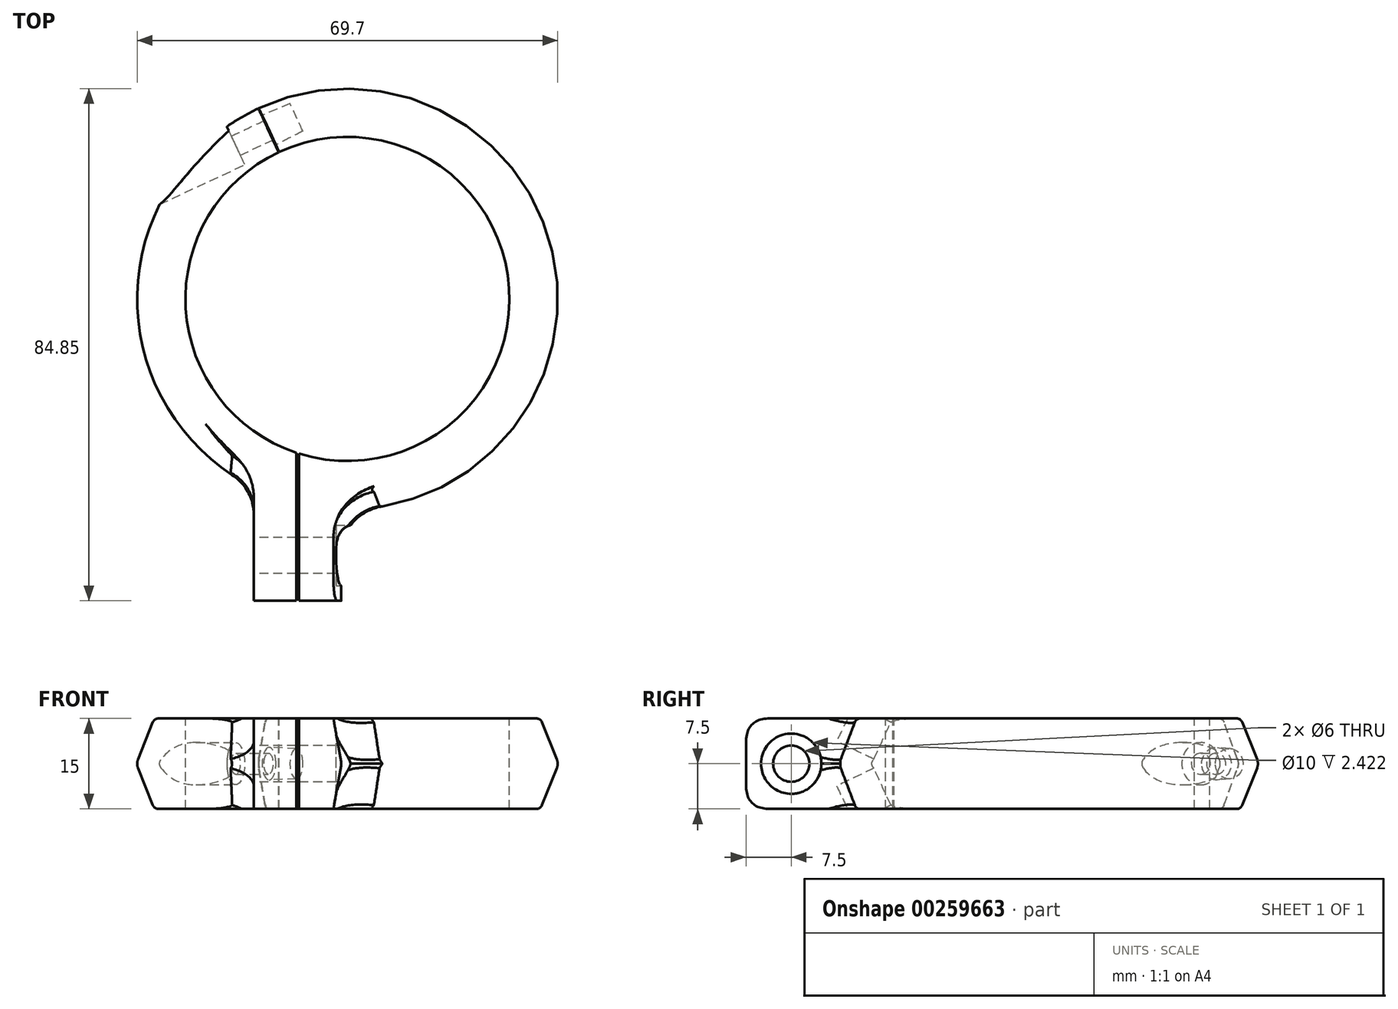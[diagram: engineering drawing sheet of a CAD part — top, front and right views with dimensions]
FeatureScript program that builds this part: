
annotation { "Feature Type Name" : "Feature", "Feature Type Description" : "" }
export const myFeature = defineFeature(function(context is Context, id is Id, definition is map)
    precondition{}
    {
        {
            var Q0;
            Q0=qCreatedBy(makeId("Front.planeOp"),FACE);
            var sketch = newSketch(context, id + "F0", { "sketchPlane" : qUnion([Q0])});
            skLineSegment(sketch, "E0.bottom", {"start": v(0, 7.5) * mm, "end": v(32, 7.5) * mm});
            skLineSegment(sketch, "E0.top", {"start": v(0, -7.5) * mm, "end": v(32, -7.5) * mm});
            skLineSegment(sketch, "E0.left", {"start": v(0, 7.5) * mm, "end": v(0, -7.5) * mm});
            skLineSegment(sketch, "E1", {"start": v(32, 7.5) * mm, "end": v(35, 0) * mm});
            skLineSegment(sketch, "E2", {"start": v(35, 0) * mm, "end": v(32, -7.5) * mm});
            skLineSegment(sketch, "E3", {"start": v(0, 0) * mm, "end": v(0, 25.95) * mm, "construction": true});
            skSolve(sketch);
        }
        {
            var Q0;
            Q0 = qSketchRegion(id + "F0", true);
            var Q1;
            Q1=sQuery(id+"F0.wireOp",EDGE,"E3");
            revolve(context, id + "F1", {"entities" : qUnion([Q0]), "axis" : qUnion([Q1]), "revolveType" : RevolveType.FULL});
        }
        {
            var Q0;
            Q0=makeQuery(id+"F1.opRevolve","SWEPT_EDGE",EDGE,{"disambiguationData":[OSD([sQuery(id+"F0.wireOp",EDGE,"E1"),sQuery(id+"F0.wireOp",EDGE,"E2")])]});
            fillet(context, id + "F2", {"entities" : qUnion([Q0]), "radius" : 2 * mm, "tangentPropagation" : true, "allowEdgeOverflow" : false});
        }
        {
            var Q0;
            {var subQ0=sQuery(id+"F0.wireOp",EDGE,"E1");var subQ1=sQuery(id+"F0.wireOp",EDGE,"E0.bottom");Q0=makeQuery(id+"F13.boolean.opBoolean","SPLIT",EDGE,{"disambiguationData":[TD([makeQuery(id+"F5.opExtrude","SWEPT_FACE",FACE,{"disambiguationData":[OSD([sQuery(id+"F4.wireOp",EDGE,"E7")])]})])],"derivedFrom":makeQuery(id+"F1.opRevolve","SWEPT_EDGE",EDGE,{"disambiguationData":[OSD([subQ1,subQ0])]})});}
            var Q1;
            Q1=makeQuery(id+"F1.opRevolve","SWEPT_EDGE",EDGE,{"disambiguationData":[OSD([sQuery(id+"F0.wireOp",EDGE,"E0.top"),sQuery(id+"F0.wireOp",EDGE,"E2")])]});
            fillet(context, id + "F3", {"entities" : qUnion([Q0, Q1]), "radius" : 1 * mm, "tangentPropagation" : true, "allowEdgeOverflow" : false});
        }
        {
            var Q0;
            Q0=qCreatedBy(makeId("Front.planeOp"),FACE);
            var sketch = newSketch(context, id + "F4", { "sketchPlane" : qUnion([Q0])});
            skLineSegment(sketch, "E4.bottom", {"start": v(-15.5, 7.5) * mm, "end": v(-1, 7.5) * mm});
            skLineSegment(sketch, "E4.top", {"start": v(-15.5, -7.5) * mm, "end": v(-1, -7.5) * mm});
            skLineSegment(sketch, "E4.left", {"start": v(-15.5, 7.5) * mm, "end": v(-15.5, -7.5) * mm});
            skLineSegment(sketch, "E4.right", {"start": v(-1, 7.5) * mm, "end": v(-1, -7.5) * mm, "construction": true});
            skLineSegment(sketch, "E5", {"start": v(-15.5, 0) * mm, "end": v(-14.18, 7.5) * mm, "construction": true});
            skLineSegment(sketch, "E6", {"start": v(-15.5, 0) * mm, "end": v(-14.18, -7.5) * mm, "construction": true});
            skLineSegment(sketch, "E7", {"start": v(-1, 0) * mm, "end": v(-2.32, 7.5) * mm});
            skLineSegment(sketch, "E8", {"start": v(-1, 0) * mm, "end": v(-2.32, -7.5) * mm});
            skSolve(sketch);
        }
        {
            var Q0;
            Q0 = qSketchRegion(id + "F4", true);
            extrude(context, id + "F5", {"entities" : qUnion([Q0]), "operationType" : NewBodyOperationType.ADD, "depth" : 50 * mm});
        }
        {
            var Q0;
            Q0=qCreatedBy(makeId("Top.planeOp"),FACE);
            var sketch = newSketch(context, id + "F6", { "sketchPlane" : qUnion([Q0])});
            skCircle(sketch, "E9", {"center": v(0, 0) * mm, "radius": 26.85 * mm});
            skSolve(sketch);
        }
        {
            var Q0;
            Q0 = qSketchRegion(id + "F6", true);
            extrude(context, id + "F7", {"entities" : qUnion([Q0]), "operationType" : NewBodyOperationType.REMOVE, "endBound" : BoundingType.SYMMETRIC, "oppositeDirection" : true, "depth" : 25 * mm});
        }
        {
            var Q0;
            Q0=qCreatedBy(makeId("Right.planeOp"),FACE);
            var sketch = newSketch(context, id + "F8", { "sketchPlane" : qUnion([Q0])});
            skLineSegment(sketch, "E10", {"start": v(25, 5) * mm, "end": v(26.85, 5) * mm});
            skLineSegment(sketch, "E11", {"start": v(26.85, 5) * mm, "end": v(28.67, 0) * mm});
            skLineSegment(sketch, "E12", {"start": v(28.67, 0) * mm, "end": v(26.85, -5) * mm});
            skLineSegment(sketch, "E13", {"start": v(26.85, -5) * mm, "end": v(25, -5) * mm});
            skLineSegment(sketch, "E14", {"start": v(25, -5) * mm, "end": v(25, 5) * mm});
            skLineSegment(sketch, "E15", {"start": v(0, 0) * mm, "end": v(0, 25.99) * mm, "construction": true});
            skSolve(sketch);
        }
        {
            var Q0;
            Q0=makeQuery(id+"F5.boolean.opBoolean","MERGE",FACE,{"derivedFrom":[makeQuery(id+"F1.opRevolve","SWEPT_FACE",FACE,{"disambiguationData":[OSD([sQuery(id+"F0.wireOp",EDGE,"E0.bottom")])]}),makeQuery(id+"F5.opExtrude","SWEPT_FACE",FACE,{"disambiguationData":[OSD([sQuery(id+"F4.wireOp",EDGE,"E4.bottom")])]})]});
            var sketch = newSketch(context, id + "F9", { "sketchPlane" : qUnion([Q0])});
            skLineSegment(sketch, "E16", {"start": v(0, 0) * mm, "end": v(-15.5, -31.05) * mm, "construction": true});
            skSolve(sketch);
        }
        {
            var Q0;
            Q0=sQuery(id+"F9.wireOp",EDGE,"E16");
            cPlane(context, id + "F10", {"entities" : qUnion([Q0]), "cplaneType" : CPlaneType.LINE_ANGLE, "offset" : 25 * mm, "angle" : 90 * degree, "width" : 150 * mm, "height" : 150 * mm});
        }
        {
            var Q0;
            Q0=qCreatedBy(id+"F10.planeOp",FACE);
            var sketch = newSketch(context, id + "F11", { "sketchPlane" : qUnion([Q0])});
            skLineSegment(sketch, "E17", {"start": v(-25, -5) * mm, "end": v(-26.85, -5) * mm});
            skLineSegment(sketch, "E18", {"start": v(-26.85, -5) * mm, "end": v(-28.67, 0) * mm});
            skLineSegment(sketch, "E19", {"start": v(-28.67, 0) * mm, "end": v(-26.85, 5) * mm});
            skLineSegment(sketch, "E20", {"start": v(-26.85, 5) * mm, "end": v(-25, 5) * mm});
            skLineSegment(sketch, "E21", {"start": v(-25, 5) * mm, "end": v(-25, -5) * mm});
            skLineSegment(sketch, "E22", {"start": v(0, 0) * mm, "end": v(0, 25.99) * mm, "construction": true});
            skSolve(sketch);
        }
        {
            var Q0;
            Q0=qCreatedBy(makeId("Top.planeOp"),FACE);
            var sketch = newSketch(context, id + "F12", { "sketchPlane" : qUnion([Q0])});
            skLineSegment(sketch, "E23", {"start": v(0, 0) * mm, "end": v(-9.92, 21.28) * mm, "construction": true});
            skLineSegment(sketch, "E24.bottom", {"start": v(-10.28, 22.17) * mm, "end": v(-10.38, 22.13) * mm});
            skLineSegment(sketch, "E24.top", {"start": v(-15.21, 32.74) * mm, "end": v(-15.3, 32.7) * mm});
            skLineSegment(sketch, "E24.left", {"start": v(-10.28, 22.17) * mm, "end": v(-15.21, 32.74) * mm});
            skLineSegment(sketch, "E24.right", {"start": v(-10.38, 22.13) * mm, "end": v(-15.3, 32.7) * mm});
            skPoint(sketch, "E24.middle", {"position": v(-12.8, 27.44) * mm});
            skLineSegment(sketch, "E25.bottom", {"start": v(-8.5, -51.4) * mm, "end": v(-8, -51.4) * mm});
            skLineSegment(sketch, "E25.top", {"start": v(-8.5, -23.49) * mm, "end": v(-8, -23.49) * mm});
            skLineSegment(sketch, "E25.left", {"start": v(-8.5, -51.4) * mm, "end": v(-8.5, -23.49) * mm});
            skLineSegment(sketch, "E25.right", {"start": v(-8, -51.4) * mm, "end": v(-8, -23.49) * mm});
            skSolve(sketch);
        }
        {
            var Q0;
            Q0 = qSketchRegion(id + "F12", true);
            extrude(context, id + "F13", {"entities" : qUnion([Q0]), "operationType" : NewBodyOperationType.REMOVE, "endBound" : BoundingType.SYMMETRIC, "oppositeDirection" : true, "depth" : 25 * mm});
        }
        {
            var Q0;
            Q0=makeQuery(id+"F5.boolean.opBoolean","INTERSECT",EDGE,{"derivedFrom":[makeQuery(id+"F1.opRevolve","SWEPT_FACE",FACE,{"disambiguationData":[OSD([sQuery(id+"F0.wireOp",EDGE,"E2")])]}),makeQuery(id+"F5.opExtrude","SWEPT_FACE",FACE,{"disambiguationData":[OSD([sQuery(id+"F4.wireOp",EDGE,"E4.left")])]})]});
            var Q1;
            Q1=makeQuery(id+"F5.boolean.opBoolean","INTERSECT",EDGE,{"derivedFrom":[makeQuery(id+"F1.opRevolve","SWEPT_FACE",FACE,{"disambiguationData":[OSD([sQuery(id+"F0.wireOp",EDGE,"E1")])]}),makeQuery(id+"F5.opExtrude","SWEPT_FACE",FACE,{"disambiguationData":[OSD([sQuery(id+"F4.wireOp",EDGE,"E4.left")])]})]});
            var Q2;
            Q2=makeQuery(id+"F5.boolean.opBoolean","INTERSECT",EDGE,{"derivedFrom":[makeQuery(id+"F1.opRevolve","SWEPT_FACE",FACE,{"disambiguationData":[OSD([sQuery(id+"F0.wireOp",EDGE,"E1")])]}),makeQuery(id+"F5.opExtrude","SWEPT_FACE",FACE,{"disambiguationData":[OSD([sQuery(id+"F4.wireOp",EDGE,"E4.left")])]})]});
            var Q3;
            Q3=makeQuery(id+"F5.boolean.opBoolean","INTERSECT",EDGE,{"derivedFrom":[makeQuery(id+"F1.opRevolve","SWEPT_FACE",FACE,{"disambiguationData":[OSD([sQuery(id+"F0.wireOp",EDGE,"E1")])]}),makeQuery(id+"F5.opExtrude","SWEPT_FACE",FACE,{"disambiguationData":[OSD([sQuery(id+"F4.wireOp",EDGE,"E7")])]})]});
            var Q4;
            Q4=makeQuery(id+"F5.boolean.opBoolean","INTERSECT",EDGE,{"derivedFrom":[makeQuery(id+"F1.opRevolve","SWEPT_FACE",FACE,{"disambiguationData":[OSD([sQuery(id+"F0.wireOp",EDGE,"E2")])]}),makeQuery(id+"F5.opExtrude","SWEPT_FACE",FACE,{"disambiguationData":[OSD([sQuery(id+"F4.wireOp",EDGE,"E8")])]})]});
            fillet(context, id + "F14", {"entities" : qUnion([Q0, Q1, Q2, Q3, Q4]), "radius" : 8 * mm, "tangentPropagation" : true, "allowEdgeOverflow" : false});
        }
        {
            var Q0;
            Q0=makeQuery(id+"F13.boolean.opBoolean","COPY",FACE,{"derivedFrom":makeQuery(id+"F13.opExtrude","SWEPT_FACE",FACE,{"disambiguationData":[OSD([sQuery(id+"F12.wireOp",EDGE,"E24.left")])]})});
            var sketch = newSketch(context, id + "F15", { "sketchPlane" : qUnion([Q0])});
            skCircle(sketch, "E26", {"center": v(-30.85, 0) * mm, "radius": 2.7 * mm});
            skLineSegment(sketch, "E27", {"start": v(-26.85, 0) * mm, "end": v(-34.85, 0) * mm, "construction": true});
            skSolve(sketch);
        }
        {
            var Q0;
            Q0=makeQuery(id+"F15.imprint","IMPRINT",FACE,{"disambiguationData":[TD([[makeQuery(id+"F15.imprint","IMPRINT",EDGE,{"derivedFrom":sQuery(id+"F15.wireOp",EDGE,"E26")}),1.0]])]});
            extrude(context, id + "F16", {"entities" : qUnion([Q0]), "operationType" : NewBodyOperationType.REMOVE, "oppositeDirection" : true, "depth" : 5 * mm, "hasDraft" : true, "draftAngle" : 2 * degree, "draftPullDirection" : true});
        }
        {
            var Q0;
            Q0=makeQuery(id+"F13.boolean.opBoolean","COPY",FACE,{"derivedFrom":makeQuery(id+"F13.opExtrude","SWEPT_FACE",FACE,{"disambiguationData":[OSD([sQuery(id+"F12.wireOp",EDGE,"E24.right")])]})});
            var sketch = newSketch(context, id + "F17", { "sketchPlane" : qUnion([Q0])});
            skLineSegment(sketch, "E28", {"start": v(26.85, 0) * mm, "end": v(34.85, 0) * mm, "construction": true});
            skCircle(sketch, "E29", {"center": v(30.85, 0) * mm, "radius": 1.75 * mm});
            skSolve(sketch);
        }
        {
            var Q0;
            Q0 = qSketchRegion(id + "F17", true);
            extrude(context, id + "F18", {"entities" : qUnion([Q0]), "operationType" : NewBodyOperationType.REMOVE, "oppositeDirection" : true, "depth" : 6 * mm});
        }
        {
            var Q0;
            Q0=makeQuery(id+"F18.boolean.opBoolean","COPY",FACE,{"derivedFrom":makeQuery(id+"F18.opExtrude","CAP_FACE",FACE,{"disambiguationData":[OSD([sQuery(id+"F17.wireOp",EDGE,"E29")])],"isStart":false})});
            var sketch = newSketch(context, id + "F19", { "sketchPlane" : qUnion([Q0])});
            skCircle(sketch, "E30", {"center": v(30.85, 0) * mm, "radius": 3.5 * mm});
            skSolve(sketch);
        }
        {
            var Q0;
            Q0 = qSketchRegion(id + "F19", true);
            extrude(context, id + "F20", {"entities" : qUnion([Q0]), "operationType" : NewBodyOperationType.REMOVE, "endBound" : BoundingType.THROUGH_ALL, "oppositeDirection" : true, "depth" : 25 * mm});
        }
        {
            var Q0;
            Q0=makeQuery(id+"F13.boolean.opBoolean","COPY",FACE,{"derivedFrom":makeQuery(id+"F13.opExtrude","SWEPT_FACE",FACE,{"disambiguationData":[OSD([sQuery(id+"F12.wireOp",EDGE,"E25.right")])]})});
            var sketch = newSketch(context, id + "F21", { "sketchPlane" : qUnion([Q0])});
            skCircle(sketch, "E31", {"center": v(42.5, 0) * mm, "radius": 3 * mm});
            skSolve(sketch);
        }
        {
            var Q0;
            Q0 = qSketchRegion(id + "F21", true);
            extrude(context, id + "F22", {"entities" : qUnion([Q0]), "operationType" : NewBodyOperationType.REMOVE, "endBound" : BoundingType.SYMMETRIC, "oppositeDirection" : true, "depth" : 25 * mm});
        }
        {
            var Q0;
            {var subQ0=sQuery(id+"F21.wireOp",EDGE,"TPeSEbKZ-4Bs4-KLaG-X3M5-nI107J7NiBt1");var subQ1=sQuery(id+"F4.wireOp",EDGE,"E4.bottom");var subQ2=sQuery(id+"F0.wireOp",EDGE,"E0.bottom");Q0=makeQuery(id+"F22.boolean.opBoolean","COPY",EDGE,{"disambiguationData":[TD([makeQuery(id+"F5.opExtrude","SWEPT_FACE",FACE,{"disambiguationData":[OSD([sQuery(id+"F4.wireOp",EDGE,"E5")])]})])],"derivedFrom":makeQuery(id+"F22.opExtrude","SWEPT_EDGE",EDGE,{"disambiguationData":[OSD([subQ2,subQ1,sQuery(id+"F12.wireOp",EDGE,"E25.right"),subQ0,sQuery(id+"F21.wireOp",EDGE,"c0wj6FnS-jEuf-wRoK-qYGN-INKrLgW8l8Zs")])]})});}
            var Q1;
            {var subQ0=sQuery(id+"F12.wireOp",EDGE,"E25.right");var subQ1=sQuery(id+"F4.wireOp",EDGE,"E4.bottom");var subQ2=sQuery(id+"F0.wireOp",EDGE,"E0.bottom");var subQ3=sQuery(id+"F21.wireOp",EDGE,"TPeSEbKZ-4Bs4-KLaG-X3M5-nI107J7NiBt1");Q1=makeQuery(id+"F22.boolean.opBoolean","COPY",EDGE,{"disambiguationData":[TD([makeQuery(id+"F5.opExtrude","SWEPT_FACE",FACE,{"disambiguationData":[OSD([sQuery(id+"F4.wireOp",EDGE,"E7")])]})])],"derivedFrom":makeQuery(id+"F22.opExtrude","SWEPT_EDGE",EDGE,{"disambiguationData":[OSD([subQ2,subQ1,subQ0,subQ3,sQuery(id+"F21.wireOp",EDGE,"c0wj6FnS-jEuf-wRoK-qYGN-INKrLgW8l8Zs")])]})});}
            var Q2;
            {var subQ0=sQuery(id+"F21.wireOp",EDGE,"TPeSEbKZ-4Bs4-KLaG-X3M5-nI107J7NiBt1");var subQ1=sQuery(id+"F12.wireOp",EDGE,"E25.right");var subQ2=sQuery(id+"F4.wireOp",EDGE,"E8");var subQ3=sQuery(id+"F4.wireOp",EDGE,"E7");var subQ4=sQuery(id+"F21.wireOp",EDGE,"iLccIwtf-qxlF-KUq4-O1UZ-VWjskxav2twh");Q2=makeQuery(id+"F22.boolean.opBoolean","COPY",EDGE,{"disambiguationData":[TD([makeQuery(id+"F5.opExtrude","SWEPT_FACE",FACE,{"disambiguationData":[OSD([subQ3])]})])],"derivedFrom":makeQuery(id+"F22.opExtrude","SWEPT_EDGE",EDGE,{"disambiguationData":[OSD([sQuery(id+"F4.wireOp",EDGE,"E4.bottom"),sQuery(id+"F4.wireOp",EDGE,"E4.top"),sQuery(id+"F4.wireOp",EDGE,"E5"),sQuery(id+"F4.wireOp",EDGE,"E6"),subQ3,subQ2,subQ1,subQ0,subQ4])]})});}
            var Q3;
            {var subQ0=sQuery(id+"F21.wireOp",EDGE,"TPeSEbKZ-4Bs4-KLaG-X3M5-nI107J7NiBt1");var subQ1=sQuery(id+"F4.wireOp",EDGE,"E6");var subQ2=sQuery(id+"F4.wireOp",EDGE,"E5");var subQ3=sQuery(id+"F21.wireOp",EDGE,"iLccIwtf-qxlF-KUq4-O1UZ-VWjskxav2twh");Q3=makeQuery(id+"F22.boolean.opBoolean","COPY",EDGE,{"disambiguationData":[TD([makeQuery(id+"F5.opExtrude","SWEPT_FACE",FACE,{"disambiguationData":[OSD([subQ2])]})])],"derivedFrom":makeQuery(id+"F22.opExtrude","SWEPT_EDGE",EDGE,{"disambiguationData":[OSD([sQuery(id+"F4.wireOp",EDGE,"E4.bottom"),sQuery(id+"F4.wireOp",EDGE,"E4.top"),subQ2,subQ1,sQuery(id+"F4.wireOp",EDGE,"E7"),sQuery(id+"F4.wireOp",EDGE,"E8"),sQuery(id+"F12.wireOp",EDGE,"E25.right"),subQ0,subQ3])]})});}
            var Q4;
            {var subQ0=sQuery(id+"F4.wireOp",EDGE,"E4.top");var subQ1=sQuery(id+"F0.wireOp",EDGE,"E0.top");var subQ2=sQuery(id+"F21.wireOp",EDGE,"iLccIwtf-qxlF-KUq4-O1UZ-VWjskxav2twh");Q4=makeQuery(id+"F22.boolean.opBoolean","COPY",EDGE,{"disambiguationData":[TD([makeQuery(id+"F5.opExtrude","SWEPT_FACE",FACE,{"disambiguationData":[OSD([sQuery(id+"F4.wireOp",EDGE,"E6")])]})])],"derivedFrom":makeQuery(id+"F22.opExtrude","SWEPT_EDGE",EDGE,{"disambiguationData":[OSD([subQ1,subQ0,sQuery(id+"F12.wireOp",EDGE,"E25.right"),subQ2,sQuery(id+"F21.wireOp",EDGE,"4cMrprGq-YRgF-T9sy-pwaC-qQGlX6H42zO3")])]})});}
            var Q5;
            {var subQ0=sQuery(id+"F12.wireOp",EDGE,"E25.right");var subQ1=sQuery(id+"F4.wireOp",EDGE,"E4.top");var subQ2=sQuery(id+"F0.wireOp",EDGE,"E0.top");var subQ3=sQuery(id+"F21.wireOp",EDGE,"iLccIwtf-qxlF-KUq4-O1UZ-VWjskxav2twh");Q5=makeQuery(id+"F22.boolean.opBoolean","COPY",EDGE,{"disambiguationData":[TD([makeQuery(id+"F5.opExtrude","SWEPT_FACE",FACE,{"disambiguationData":[OSD([sQuery(id+"F4.wireOp",EDGE,"E8")])]})])],"derivedFrom":makeQuery(id+"F22.opExtrude","SWEPT_EDGE",EDGE,{"disambiguationData":[OSD([subQ2,subQ1,subQ0,subQ3,sQuery(id+"F21.wireOp",EDGE,"4cMrprGq-YRgF-T9sy-pwaC-qQGlX6H42zO3")])]})});}
            var Q6;
            Q6=makeQuery(id+"F5.opExtrude","SWEPT_EDGE",EDGE,{"disambiguationData":[OSD([sQuery(id+"F4.wireOp",EDGE,"E7"),sQuery(id+"F4.wireOp",EDGE,"E8")])]});
            var Q7;
            {var subQ0=sQuery(id+"F21.wireOp",EDGE,"TPeSEbKZ-4Bs4-KLaG-X3M5-nI107J7NiBt1");var subQ1=sQuery(id+"F4.wireOp",EDGE,"E4.bottom");var subQ2=sQuery(id+"F0.wireOp",EDGE,"E0.bottom");Q7=makeQuery(id+"F22.boolean.opBoolean","COPY",EDGE,{"disambiguationData":[TD([makeQuery(id+"F5.opExtrude","SWEPT_FACE",FACE,{"disambiguationData":[OSD([sQuery(id+"F4.wireOp",EDGE,"E4.left")])]})])],"derivedFrom":makeQuery(id+"F22.opExtrude","SWEPT_EDGE",EDGE,{"disambiguationData":[OSD([subQ2,subQ1,sQuery(id+"F12.wireOp",EDGE,"E25.right"),subQ0,sQuery(id+"F21.wireOp",EDGE,"c0wj6FnS-jEuf-wRoK-qYGN-INKrLgW8l8Zs")])]})});}
            var Q8;
            {var subQ0=sQuery(id+"F4.wireOp",EDGE,"E4.left");var subQ1=sQuery(id+"F21.wireOp",EDGE,"TPeSEbKZ-4Bs4-KLaG-X3M5-nI107J7NiBt1");var subQ2=sQuery(id+"F21.wireOp",EDGE,"iLccIwtf-qxlF-KUq4-O1UZ-VWjskxav2twh");Q8=makeQuery(id+"F22.boolean.opBoolean","COPY",EDGE,{"disambiguationData":[TD([makeQuery(id+"F5.opExtrude","SWEPT_FACE",FACE,{"disambiguationData":[OSD([subQ0])]})])],"derivedFrom":makeQuery(id+"F22.opExtrude","SWEPT_EDGE",EDGE,{"disambiguationData":[OSD([sQuery(id+"F4.wireOp",EDGE,"E4.bottom"),sQuery(id+"F4.wireOp",EDGE,"E4.top"),subQ0,sQuery(id+"F4.wireOp",EDGE,"E7"),sQuery(id+"F4.wireOp",EDGE,"E8"),sQuery(id+"F12.wireOp",EDGE,"E25.right"),subQ1,subQ2])]})});}
            var Q9;
            {var subQ0=sQuery(id+"F4.wireOp",EDGE,"E4.top");var subQ1=sQuery(id+"F0.wireOp",EDGE,"E0.top");var subQ2=sQuery(id+"F21.wireOp",EDGE,"iLccIwtf-qxlF-KUq4-O1UZ-VWjskxav2twh");Q9=makeQuery(id+"F22.boolean.opBoolean","COPY",EDGE,{"disambiguationData":[TD([makeQuery(id+"F5.opExtrude","SWEPT_FACE",FACE,{"disambiguationData":[OSD([sQuery(id+"F4.wireOp",EDGE,"E4.left")])]})])],"derivedFrom":makeQuery(id+"F22.opExtrude","SWEPT_EDGE",EDGE,{"disambiguationData":[OSD([subQ1,subQ0,sQuery(id+"F12.wireOp",EDGE,"E25.right"),subQ2,sQuery(id+"F21.wireOp",EDGE,"4cMrprGq-YRgF-T9sy-pwaC-qQGlX6H42zO3")])]})});}
            fillet(context, id + "F23", {"entities" : qUnion([Q0, Q1, Q2, Q3, Q4, Q5, Q6, Q7, Q8, Q9]), "radius" : 2 * mm, "tangentPropagation" : true, "rho" : 0.5, "crossSection" : FilletCrossSection.CONIC, "allowEdgeOverflow" : false});
        }
        {
            var Q0;
            Q0=qCreatedBy(makeId("Right.planeOp"),FACE);
            var sketch = newSketch(context, id + "F24", { "sketchPlane" : qUnion([Q0])});
            skCircle(sketch, "E32", {"center": v(-42.5, 0) * mm, "radius": 5 * mm});
            skSolve(sketch);
        }
        {
            var Q0;
            Q0 = qSketchRegion(id + "F24", true);
            var Q1;
            Q1=makeQuery(id+"F5.opExtrude","SWEPT_FACE",FACE,{"disambiguationData":[OSD([sQuery(id+"F4.wireOp",EDGE,"E8")])]});
            var Q2;
            Q2=makeQuery(id+"F13.boolean.opBoolean","SPLIT",BODY,{"disambiguationData":[OD(1.0)],"derivedFrom":makeQuery(id+"F1.opRevolve","SWEPT_BODY",BODY,{"disambiguationData":[OSD([sQuery(id+"F0.wireOp",EDGE,"E0.bottom"),sQuery(id+"F0.wireOp",EDGE,"E0.top"),sQuery(id+"F0.wireOp",EDGE,"E0.left"),sQuery(id+"F0.wireOp",EDGE,"E1"),sQuery(id+"F0.wireOp",EDGE,"E2")])]})});
            extrude(context, id + "F25", {"entities" : qUnion([Q0]), "operationType" : NewBodyOperationType.REMOVE, "endBound" : BoundingType.SYMMETRIC, "oppositeDirection" : true, "endBoundEntityFace" : qUnion([Q1]), "endBoundEntityBody" : qUnion([Q2]), "depth" : (1.88 + 1.88) * mm});
        }
        {
            var Q0;
            {var subQ0=sQuery(id+"F4.wireOp",EDGE,"E7");var subQ1=sQuery(id+"F4.wireOp",EDGE,"E4.bottom");Q0=makeQuery(id+"F13.boolean.opBoolean","SPLIT",EDGE,{"disambiguationData":[TD([makeQuery(id+"F5.opExtrude","SWEPT_FACE",FACE,{"disambiguationData":[OSD([subQ0])]})])],"derivedFrom":makeQuery(id+"F5.opExtrude","CAP_EDGE",EDGE,{"disambiguationData":[OSD([subQ1])],"isStart":false})});}
            var Q1;
            {var subQ0=sQuery(id+"F4.wireOp",EDGE,"E4.left");var subQ1=sQuery(id+"F4.wireOp",EDGE,"E4.bottom");Q1=makeQuery(id+"F13.boolean.opBoolean","SPLIT",EDGE,{"disambiguationData":[TD([makeQuery(id+"F5.opExtrude","SWEPT_FACE",FACE,{"disambiguationData":[OSD([subQ0])]})])],"derivedFrom":makeQuery(id+"F5.opExtrude","CAP_EDGE",EDGE,{"disambiguationData":[OSD([subQ1])],"isStart":false})});}
            var Q2;
            {var subQ0=sQuery(id+"F4.wireOp",EDGE,"E4.left");var subQ1=sQuery(id+"F4.wireOp",EDGE,"E4.top");Q2=makeQuery(id+"F13.boolean.opBoolean","SPLIT",EDGE,{"disambiguationData":[TD([makeQuery(id+"F5.opExtrude","SWEPT_FACE",FACE,{"disambiguationData":[OSD([subQ0])]})])],"derivedFrom":makeQuery(id+"F5.opExtrude","CAP_EDGE",EDGE,{"disambiguationData":[OSD([subQ1])],"isStart":false})});}
            var Q3;
            {var subQ0=sQuery(id+"F4.wireOp",EDGE,"E8");var subQ1=sQuery(id+"F4.wireOp",EDGE,"E4.top");Q3=makeQuery(id+"F13.boolean.opBoolean","SPLIT",EDGE,{"disambiguationData":[TD([makeQuery(id+"F5.opExtrude","SWEPT_FACE",FACE,{"disambiguationData":[OSD([subQ0])]})])],"derivedFrom":makeQuery(id+"F5.opExtrude","CAP_EDGE",EDGE,{"disambiguationData":[OSD([subQ1])],"isStart":false})});}
            fillet(context, id + "F26", {"entities" : qUnion([Q0, Q1, Q2, Q3]), "radius" : 4 * mm, "rho" : 0.5, "crossSection" : FilletCrossSection.CONIC, "allowEdgeOverflow" : false});
        }
    });
